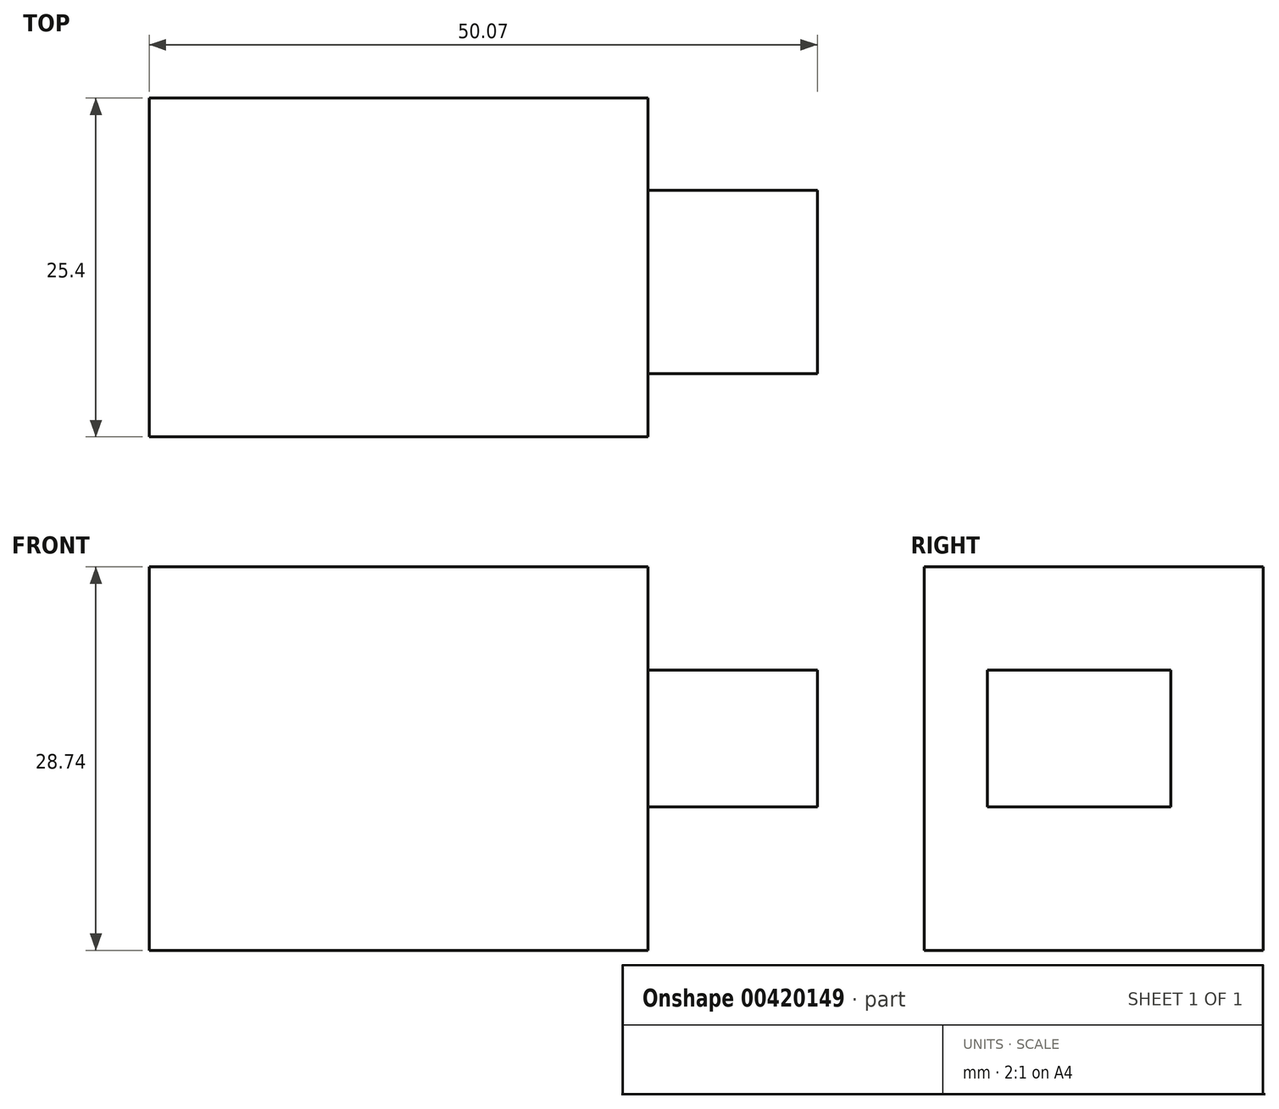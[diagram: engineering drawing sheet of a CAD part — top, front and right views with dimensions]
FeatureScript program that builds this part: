
annotation { "Feature Type Name" : "Feature", "Feature Type Description" : "" }
export const myFeature = defineFeature(function(context is Context, id is Id, definition is map)
    precondition{}
    {
        {
            var Q0;
            Q0=qCreatedBy(makeId("Front.planeOp"),FACE);
            var sketch = newSketch(context, id + "F0", { "sketchPlane" : qUnion([Q0])});
            skLineSegment(sketch, "E0.bottom", {"start": v(0, 0) * mm, "end": v(37.37, 0) * mm});
            skLineSegment(sketch, "E0.top", {"start": v(0, -28.74) * mm, "end": v(37.37, -28.74) * mm});
            skLineSegment(sketch, "E0.left", {"start": v(0, 0) * mm, "end": v(0, -28.74) * mm});
            skLineSegment(sketch, "E0.right", {"start": v(37.37, 0) * mm, "end": v(37.37, -28.74) * mm});
            skSolve(sketch);
        }
        {
            var Q0;
            Q0 = qSketchRegion(id + "F0", true);
            extrude(context, id + "F1", {"entities" : qUnion([Q0]), "depth" : 25.4 * mm});
        }
        {
            var Q0;
            Q0=makeQuery(id+"F1.opExtrude","SWEPT_FACE",FACE,{"disambiguationData":[OSD([sQuery(id+"F0.wireOp",EDGE,"E0.bottom")])]});
            var sketch = newSketch(context, id + "F2", { "sketchPlane" : qUnion([Q0])});
            skCircle(sketch, "E1", {"center": v(18.68, -12.7) * mm, "radius": 12.7 * mm});
            skPoint(sketch, "E1.centerSnap0", {"position": v(18.68, 0) * mm});
            skPoint(sketch, "E1.centerSnap1", {"position": v(37.37, -12.7) * mm});
            skSolve(sketch);
        }
        {
            var Q0;
            {var subQ0=sQuery(id+"F2.wireOp",EDGE,"E1");var subQ1=sQuery(id+"F0.wireOp",EDGE,"E0.bottom");var subQ2=makeQuery(id+"F2.imprint","INTERSECT",VERTEX,{"derivedFrom":[makeQuery(id+"F1.opExtrude","CAP_EDGE",EDGE,{"disambiguationData":[OSD([subQ1])],"isStart":true}),subQ0]});Q0=makeQuery(id+"F2.imprint","IMPRINT",FACE,{"disambiguationData":[TD([[makeQuery(id+"F2.imprint","IMPRINT",EDGE,{"disambiguationData":[TD([[subQ2,-1.0]])],"derivedFrom":subQ0}),1.0]])]});}
            var Q1;
            Q1=sQuery(id+"F2.wireOp",EDGE,"E1");
            extrude(context, id + "F3", {"entities" : qUnion([Q0]), "bodyType" : ToolBodyType.SURFACE, "operationType" : NewBodyOperationType.ADD, "surfaceEntities" : qUnion([Q1]), "depth" : 50.8 * mm});
        }
        {
            var Q0;
            Q0=makeQuery(id+"F1.opExtrude","SWEPT_FACE",FACE,{"disambiguationData":[OSD([sQuery(id+"F0.wireOp",EDGE,"E0.right")])]});
            var sketch = newSketch(context, id + "F4", { "sketchPlane" : qUnion([Q0])});
            skLineSegment(sketch, "E2.bottom", {"start": v(-6.9, -7.73) * mm, "end": v(-20.66, -7.73) * mm});
            skLineSegment(sketch, "E2.top", {"start": v(-6.9, -17.98) * mm, "end": v(-20.66, -17.98) * mm});
            skLineSegment(sketch, "E2.left", {"start": v(-6.9, -7.73) * mm, "end": v(-6.9, -17.98) * mm});
            skLineSegment(sketch, "E2.right", {"start": v(-20.66, -7.73) * mm, "end": v(-20.66, -17.98) * mm});
            skPoint(sketch, "E2.middle", {"position": v(-13.78, -12.86) * mm});
            skSolve(sketch);
        }
        {
            var Q0;
            Q0 = qSketchRegion(id + "F4", true);
            extrude(context, id + "F5", {"entities" : qUnion([Q0]), "operationType" : NewBodyOperationType.ADD, "depth" : 12.7 * mm});
        }
    });
